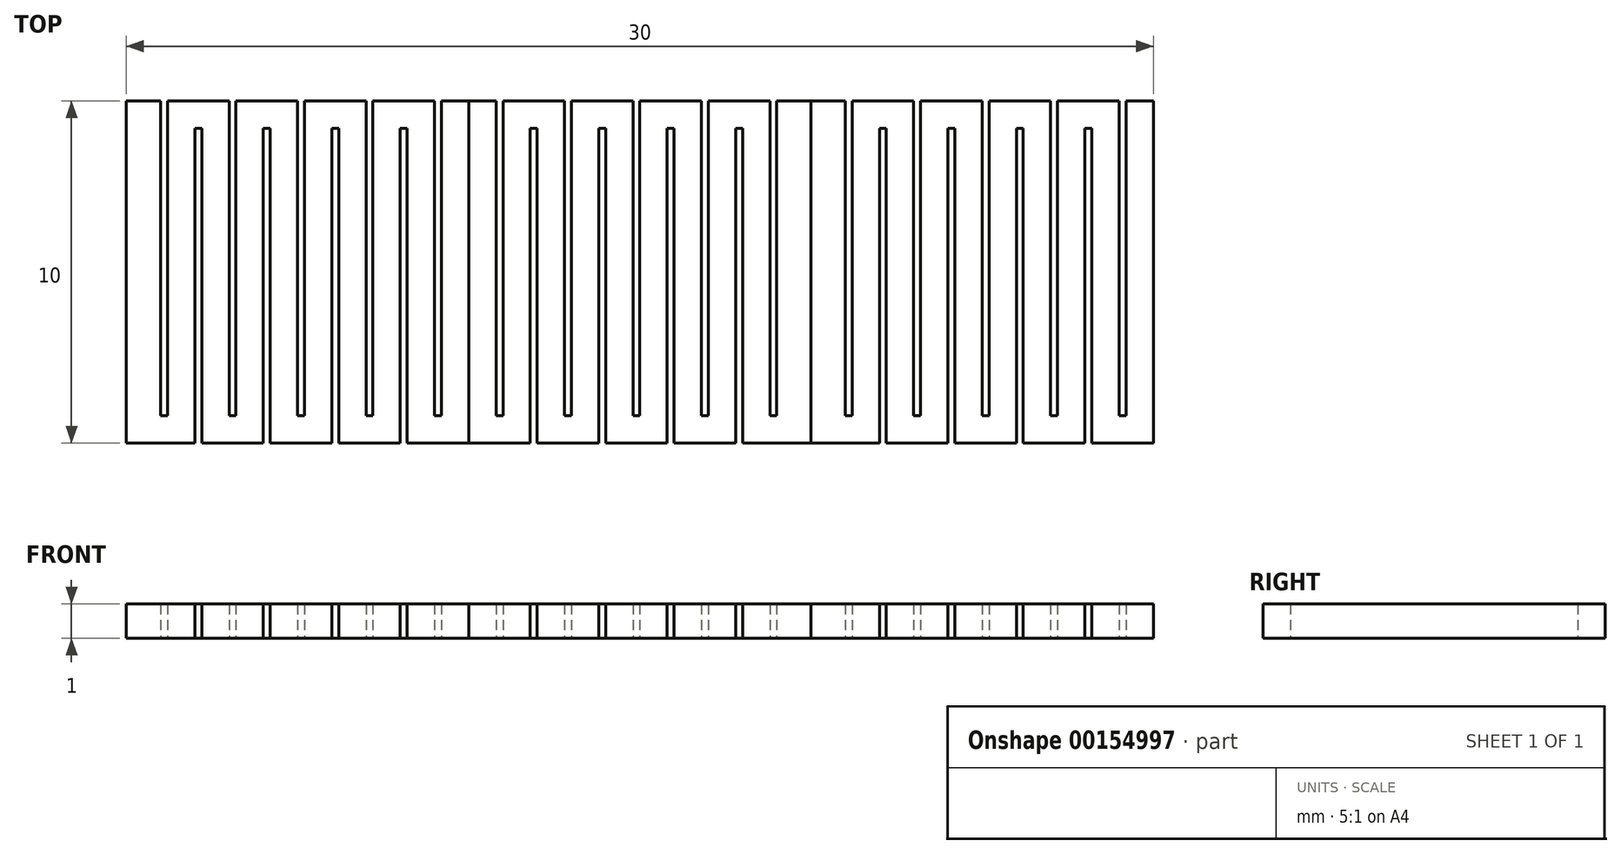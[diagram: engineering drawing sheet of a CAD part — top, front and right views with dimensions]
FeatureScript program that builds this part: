
annotation { "Feature Type Name" : "Feature", "Feature Type Description" : "" }
export const myFeature = defineFeature(function(context is Context, id is Id, definition is map)
    precondition{}
    {
        {
            var Q0;
            Q0=qCreatedBy(makeId("Top.planeOp"),FACE);
            var sketch = newSketch(context, id + "F0", { "sketchPlane" : qUnion([Q0])});
            skLineSegment(sketch, "E0.bottom", {"start": v(5, 5) * mm, "end": v(4, 5) * mm});
            skLineSegment(sketch, "E0.top", {"start": v(5, -5) * mm, "end": v(3, -5) * mm});
            skLineSegment(sketch, "E0.left", {"start": v(5, 5) * mm, "end": v(5, -5) * mm});
            skLineSegment(sketch, "E0.right", {"start": v(-5, 5) * mm, "end": v(-5, -5) * mm});
            skPoint(sketch, "E0.middle", {"position": v(0, 0) * mm});
            skLineSegment(sketch, "E1", {"start": v(-4.2, 5) * mm, "end": v(-4.2, -4.2) * mm});
            skLineSegment(sketch, "E2", {"start": v(-4.2, -4.2) * mm, "end": v(-4, -4.2) * mm});
            skLineSegment(sketch, "E3", {"start": v(-4, -4.2) * mm, "end": v(-4, 5) * mm});
            skLineSegment(sketch, "E4", {"start": v(-4, 5) * mm, "end": v(-2.2, 5) * mm});
            skLineSegment(sketch, "E5", {"start": v(2.8, -5) * mm, "end": v(2.8, 4.2) * mm});
            skLineSegment(sketch, "E6", {"start": v(2.8, 4.2) * mm, "end": v(3, 4.2) * mm});
            skLineSegment(sketch, "E7", {"start": v(3, 4.2) * mm, "end": v(3, -5) * mm});
            skLineSegment(sketch, "E8.1.0.0", {"start": v(-2.2, 5) * mm, "end": v(-2.2, -4.2) * mm});
            skLineSegment(sketch, "E8.1.0.1", {"start": v(-2, -4.2) * mm, "end": v(-2, 5) * mm});
            skLineSegment(sketch, "E8.1.0.2", {"start": v(-2.2, -4.2) * mm, "end": v(-2, -4.2) * mm});
            skLineSegment(sketch, "E8.2.0.0", {"start": v(-0.2, 5) * mm, "end": v(-0.2, -4.2) * mm});
            skLineSegment(sketch, "E8.2.0.1", {"start": v(0, -4.2) * mm, "end": v(0, 5) * mm});
            skLineSegment(sketch, "E8.2.0.2", {"start": v(-0.2, -4.2) * mm, "end": v(0, -4.2) * mm});
            skLineSegment(sketch, "E8.3.0.0", {"start": v(1.8, 5) * mm, "end": v(1.8, -4.2) * mm});
            skLineSegment(sketch, "E8.3.0.1", {"start": v(2, -4.2) * mm, "end": v(2, 5) * mm});
            skLineSegment(sketch, "E8.3.0.2", {"start": v(1.8, -4.2) * mm, "end": v(2, -4.2) * mm});
            skLineSegment(sketch, "E8.4.0.0", {"start": v(3.8, 5) * mm, "end": v(3.8, -4.2) * mm});
            skLineSegment(sketch, "E8.4.0.1", {"start": v(4, -4.2) * mm, "end": v(4, 5) * mm});
            skLineSegment(sketch, "E8.4.0.2", {"start": v(3.8, -4.2) * mm, "end": v(4, -4.2) * mm});
            skLineSegment(sketch, "E8.direction1", {"start": v(-4.2, -4.2) * mm, "end": v(-2.2, -4.2) * mm, "construction": true});
            skLineSegment(sketch, "E9.1.0.0", {"start": v(0.8, -5) * mm, "end": v(0.8, 4.2) * mm});
            skLineSegment(sketch, "E9.1.0.1", {"start": v(1, 4.2) * mm, "end": v(1, -5) * mm});
            skLineSegment(sketch, "E9.1.0.2", {"start": v(0.8, 4.2) * mm, "end": v(1, 4.2) * mm});
            skLineSegment(sketch, "E9.2.0.0", {"start": v(-1.2, -5) * mm, "end": v(-1.2, 4.2) * mm});
            skLineSegment(sketch, "E9.2.0.1", {"start": v(-1, 4.2) * mm, "end": v(-1, -5) * mm});
            skLineSegment(sketch, "E9.2.0.2", {"start": v(-1.2, 4.2) * mm, "end": v(-1, 4.2) * mm});
            skLineSegment(sketch, "E9.3.0.0", {"start": v(-3.2, -5) * mm, "end": v(-3.2, 4.2) * mm});
            skLineSegment(sketch, "E9.3.0.1", {"start": v(-3, 4.2) * mm, "end": v(-3, -5) * mm});
            skLineSegment(sketch, "E9.3.0.2", {"start": v(-3.2, 4.2) * mm, "end": v(-3, 4.2) * mm});
            skLineSegment(sketch, "E9.direction1", {"start": v(2.8, -5) * mm, "end": v(1, -5) * mm, "construction": true});
            skLineSegment(sketch, "E10.trimOffspring", {"start": v(-4.2, 5) * mm, "end": v(-5, 5) * mm});
            skLineSegment(sketch, "E11.trimOffspring", {"start": v(-2, 5) * mm, "end": v(-0.2, 5) * mm});
            skLineSegment(sketch, "E12.trimOffspring", {"start": v(1.8, 5) * mm, "end": v(0.89, 5) * mm});
            skLineSegment(sketch, "E13.trimOffspring", {"start": v(0, 5) * mm, "end": v(0.89, 5) * mm});
            skLineSegment(sketch, "E14.trimOffspring", {"start": v(3.8, 5) * mm, "end": v(2, 5) * mm});
            skLineSegment(sketch, "E15.trimOffspring", {"start": v(-3.2, -5) * mm, "end": v(-5, -5) * mm});
            skLineSegment(sketch, "E16.trimOffspring", {"start": v(-1.2, -5) * mm, "end": v(-3, -5) * mm});
            skLineSegment(sketch, "E17.trimOffspring", {"start": v(2.8, -5) * mm, "end": v(1, -5) * mm});
            skLineSegment(sketch, "E18.trimOffspring", {"start": v(0.8, -5) * mm, "end": v(-1, -5) * mm});
            skSolve(sketch);
        }
        {
            var Q0;
            Q0 = qSketchRegion(id + "F0", true);
            extrude(context, id + "F1", {"entities" : qUnion([Q0]), "depth" : 1 * mm});
        }
        {
            var Q0;
            Q0=makeQuery(id+"F1.opExtrude","SWEPT_BODY",BODY,{"disambiguationData":[OSD([sQuery(id+"F0.wireOp",EDGE,"E0.bottom"),sQuery(id+"F0.wireOp",EDGE,"E0.top"),sQuery(id+"F0.wireOp",EDGE,"E0.left"),sQuery(id+"F0.wireOp",EDGE,"E0.right"),sQuery(id+"F0.wireOp",EDGE,"E1"),sQuery(id+"F0.wireOp",EDGE,"E2"),sQuery(id+"F0.wireOp",EDGE,"E3"),sQuery(id+"F0.wireOp",EDGE,"E4"),sQuery(id+"F0.wireOp",EDGE,"E5"),sQuery(id+"F0.wireOp",EDGE,"E6"),sQuery(id+"F0.wireOp",EDGE,"E7"),sQuery(id+"F0.wireOp",EDGE,"E8.1.0.0"),sQuery(id+"F0.wireOp",EDGE,"E8.1.0.1"),sQuery(id+"F0.wireOp",EDGE,"E8.1.0.2"),sQuery(id+"F0.wireOp",EDGE,"E8.2.0.0"),sQuery(id+"F0.wireOp",EDGE,"E8.2.0.1"),sQuery(id+"F0.wireOp",EDGE,"E8.2.0.2"),sQuery(id+"F0.wireOp",EDGE,"E8.3.0.0"),sQuery(id+"F0.wireOp",EDGE,"E8.3.0.1"),sQuery(id+"F0.wireOp",EDGE,"E8.3.0.2"),sQuery(id+"F0.wireOp",EDGE,"E8.4.0.0"),sQuery(id+"F0.wireOp",EDGE,"E8.4.0.1"),sQuery(id+"F0.wireOp",EDGE,"E8.4.0.2"),sQuery(id+"F0.wireOp",EDGE,"E9.1.0.0"),sQuery(id+"F0.wireOp",EDGE,"E9.1.0.1"),sQuery(id+"F0.wireOp",EDGE,"E9.1.0.2"),sQuery(id+"F0.wireOp",EDGE,"E9.2.0.0"),sQuery(id+"F0.wireOp",EDGE,"E9.2.0.1"),sQuery(id+"F0.wireOp",EDGE,"E9.2.0.2"),sQuery(id+"F0.wireOp",EDGE,"E9.3.0.0"),sQuery(id+"F0.wireOp",EDGE,"E9.3.0.1"),sQuery(id+"F0.wireOp",EDGE,"E9.3.0.2"),sQuery(id+"F0.wireOp",EDGE,"E10.trimOffspring"),sQuery(id+"F0.wireOp",EDGE,"E11.trimOffspring"),sQuery(id+"F0.wireOp",EDGE,"E12.trimOffspring"),sQuery(id+"F0.wireOp",EDGE,"E13.trimOffspring"),sQuery(id+"F0.wireOp",EDGE,"E14.trimOffspring"),sQuery(id+"F0.wireOp",EDGE,"E15.trimOffspring"),sQuery(id+"F0.wireOp",EDGE,"E16.trimOffspring"),sQuery(id+"F0.wireOp",EDGE,"E17.trimOffspring"),sQuery(id+"F0.wireOp",EDGE,"E18.trimOffspring")])]});
            var Q1;
            Q1=makeQuery(id+"F1.opExtrude","SWEPT_FACE",FACE,{"disambiguationData":[OSD([sQuery(id+"F0.wireOp",EDGE,"E0.left")])]});
            mirror(context, id + "F2", {"entities" : qUnion([Q0]), "mirrorPlane" : qUnion([Q1])});
        }
        {
            var Q0;
            Q0=makeQuery(id+"F1.opExtrude","SWEPT_BODY",BODY,{"disambiguationData":[OSD([sQuery(id+"F0.wireOp",EDGE,"E0.bottom"),sQuery(id+"F0.wireOp",EDGE,"E0.top"),sQuery(id+"F0.wireOp",EDGE,"E0.left"),sQuery(id+"F0.wireOp",EDGE,"E0.right"),sQuery(id+"F0.wireOp",EDGE,"E1"),sQuery(id+"F0.wireOp",EDGE,"E2"),sQuery(id+"F0.wireOp",EDGE,"E3"),sQuery(id+"F0.wireOp",EDGE,"E4"),sQuery(id+"F0.wireOp",EDGE,"E5"),sQuery(id+"F0.wireOp",EDGE,"E6"),sQuery(id+"F0.wireOp",EDGE,"E7"),sQuery(id+"F0.wireOp",EDGE,"E8.1.0.0"),sQuery(id+"F0.wireOp",EDGE,"E8.1.0.1"),sQuery(id+"F0.wireOp",EDGE,"E8.1.0.2"),sQuery(id+"F0.wireOp",EDGE,"E8.2.0.0"),sQuery(id+"F0.wireOp",EDGE,"E8.2.0.1"),sQuery(id+"F0.wireOp",EDGE,"E8.2.0.2"),sQuery(id+"F0.wireOp",EDGE,"E8.3.0.0"),sQuery(id+"F0.wireOp",EDGE,"E8.3.0.1"),sQuery(id+"F0.wireOp",EDGE,"E8.3.0.2"),sQuery(id+"F0.wireOp",EDGE,"E8.4.0.0"),sQuery(id+"F0.wireOp",EDGE,"E8.4.0.1"),sQuery(id+"F0.wireOp",EDGE,"E8.4.0.2"),sQuery(id+"F0.wireOp",EDGE,"E9.1.0.0"),sQuery(id+"F0.wireOp",EDGE,"E9.1.0.1"),sQuery(id+"F0.wireOp",EDGE,"E9.1.0.2"),sQuery(id+"F0.wireOp",EDGE,"E9.2.0.0"),sQuery(id+"F0.wireOp",EDGE,"E9.2.0.1"),sQuery(id+"F0.wireOp",EDGE,"E9.2.0.2"),sQuery(id+"F0.wireOp",EDGE,"E9.3.0.0"),sQuery(id+"F0.wireOp",EDGE,"E9.3.0.1"),sQuery(id+"F0.wireOp",EDGE,"E9.3.0.2"),sQuery(id+"F0.wireOp",EDGE,"E10.trimOffspring"),sQuery(id+"F0.wireOp",EDGE,"E11.trimOffspring"),sQuery(id+"F0.wireOp",EDGE,"E12.trimOffspring"),sQuery(id+"F0.wireOp",EDGE,"E13.trimOffspring"),sQuery(id+"F0.wireOp",EDGE,"E14.trimOffspring"),sQuery(id+"F0.wireOp",EDGE,"E15.trimOffspring"),sQuery(id+"F0.wireOp",EDGE,"E16.trimOffspring"),sQuery(id+"F0.wireOp",EDGE,"E17.trimOffspring"),sQuery(id+"F0.wireOp",EDGE,"E18.trimOffspring")])]});
            var Q1;
            Q1=makeQuery(id+"F1.opExtrude","SWEPT_FACE",FACE,{"disambiguationData":[OSD([sQuery(id+"F0.wireOp",EDGE,"E0.right")])]});
            mirror(context, id + "F3", {"entities" : qUnion([Q0]), "mirrorPlane" : qUnion([Q1])});
        }
    });
